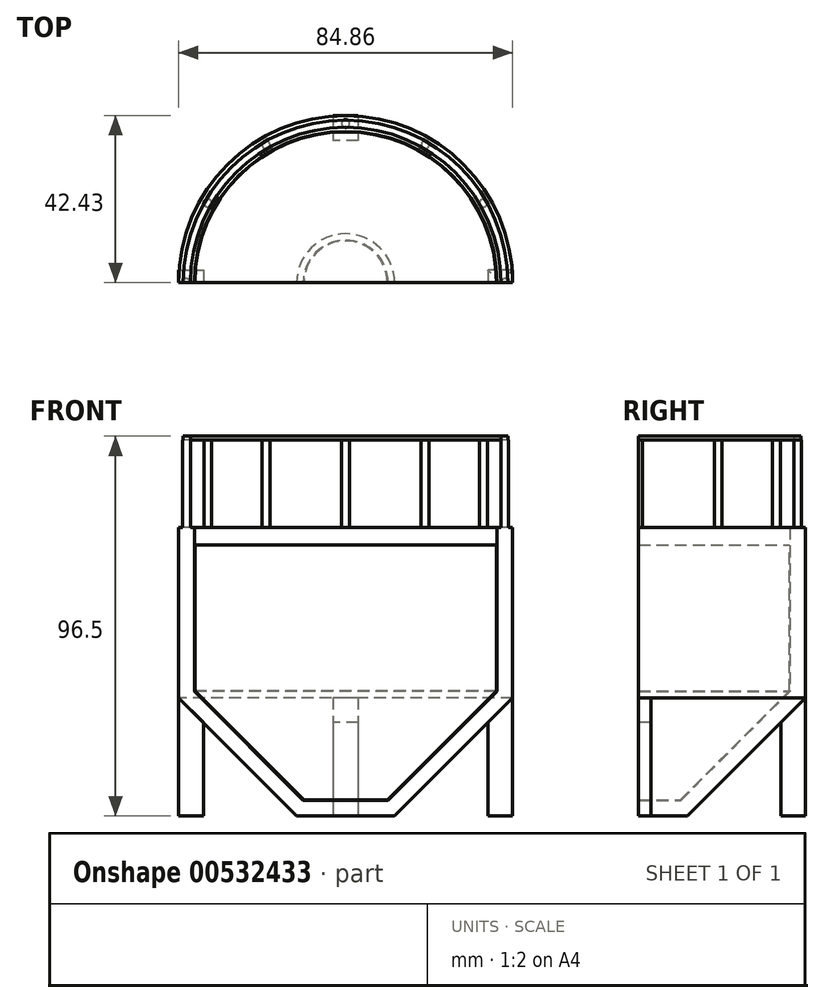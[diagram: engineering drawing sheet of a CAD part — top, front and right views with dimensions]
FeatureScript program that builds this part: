
annotation { "Feature Type Name" : "Feature", "Feature Type Description" : "" }
export const myFeature = defineFeature(function(context is Context, id is Id, definition is map)
    precondition{}
    {
        {
            var Q0;
            Q0=qCreatedBy(makeId("Top.planeOp"),FACE);
            var sketch = newSketch(context, id + "F0", { "sketchPlane" : qUnion([Q0])});
            skLineSegment(sketch, "E0", {"start": v(-29.35, 0) * mm, "end": v(28.84, 0) * mm, "construction": true});
            skLineSegment(sketch, "E1", {"start": v(0, 29.6) * mm, "end": v(0, -29.2) * mm, "construction": true});
            skLineSegment(sketch, "E2.bottom", {"start": v(30, 30) * mm, "end": v(-30, 30) * mm, "construction": true});
            skLineSegment(sketch, "E2.top", {"start": v(30, -30) * mm, "end": v(-30, -30) * mm, "construction": true});
            skLineSegment(sketch, "E2.left", {"start": v(30, 30) * mm, "end": v(30, -30) * mm, "construction": true});
            skLineSegment(sketch, "E2.right", {"start": v(-30, 30) * mm, "end": v(-30, -30) * mm, "construction": true});
            skPoint(sketch, "E2.middle", {"position": v(0, 0) * mm});
            skCircle(sketch, "E3", {"center": v(0, 0) * mm, "radius": 42.43 * mm});
            skSolve(sketch);
        }
        {
            var Q0;
            Q0 = qSketchRegion(id + "F0", true);
            extrude(context, id + "F1", {"entities" : qUnion([Q0]), "depth" : 73.3 * mm, "offsetDistance" : 25 * mm});
        }
        {
            var Q0;
            Q0=makeQuery(id+"F1.opExtrude","CAP_FACE",FACE,{"disambiguationData":[OSD([sQuery(id+"F0.wireOp",EDGE,"E3")])],"isStart":true});
            chamfer(context, id + "F2", {"entities" : qUnion([Q0]), "width" : 30 * mm, "tangentPropagation" : true});
        }
        {
            var Q0;
            Q0=makeQuery(id+"F1.opExtrude","CAP_FACE",FACE,{"disambiguationData":[OSD([sQuery(id+"F0.wireOp",EDGE,"E3")])],"isStart":false});
            shell(context, id + "F3", {"entities" : qUnion([Q0]), "thickness" : 4 * mm});
        }
        {
            var Q0;
            Q0=makeQuery(id+"F1.opExtrude","CAP_FACE",FACE,{"disambiguationData":[OSD([sQuery(id+"F0.wireOp",EDGE,"E3")])],"isStart":false});
            var sketch = newSketch(context, id + "F4", { "sketchPlane" : qUnion([Q0])});
            skCircle(sketch, "E4.0.0", {"center": v(0, 0) * mm, "radius": 42.43 * mm, "construction": true});
            skCircle(sketch, "E5.0", {"center": v(0, 0) * mm, "radius": 40.43 * mm, "construction": true});
            skCircle(sketch, "E6", {"center": v(0, 40.43) * mm, "radius": 1 * mm});
            skCircle(sketch, "E7.1.0", {"center": v(-20.21, 35.01) * mm, "radius": 1 * mm});
            skCircle(sketch, "E7.2.0", {"center": v(-35.01, 20.21) * mm, "radius": 1 * mm});
            skCircle(sketch, "E7.3.0", {"center": v(-40.43, 0) * mm, "radius": 1 * mm});
            skCircle(sketch, "E7.4.0", {"center": v(-35.01, -20.21) * mm, "radius": 1 * mm});
            skCircle(sketch, "E7.5.0", {"center": v(-20.21, -35.01) * mm, "radius": 1 * mm});
            skCircle(sketch, "E7.6.0", {"center": v(0, -40.43) * mm, "radius": 1 * mm});
            skCircle(sketch, "E7.7.0", {"center": v(20.21, -35.01) * mm, "radius": 1 * mm});
            skCircle(sketch, "E7.8.0", {"center": v(35.01, -20.21) * mm, "radius": 1 * mm});
            skCircle(sketch, "E7.9.0", {"center": v(40.43, 0) * mm, "radius": 1 * mm});
            skLineSegment(sketch, "E7.anchor1", {"start": v(0, 0) * mm, "end": v(0, 40.43) * mm, "construction": true});
            skLineSegment(sketch, "E7.anchor2", {"start": v(0, 0) * mm, "end": v(20.21, 35.01) * mm, "construction": true});
            skCircle(sketch, "E8.1.10.0", {"center": v(35.01, 20.21) * mm, "radius": 1 * mm});
            skCircle(sketch, "E9.1.11.0", {"center": v(20.21, 35.01) * mm, "radius": 1 * mm});
            skSolve(sketch);
        }
        {
            var Q0;
            Q0 = qSketchRegion(id + "F4", true);
            extrude(context, id + "F5", {"entities" : qUnion([Q0]), "operationType" : NewBodyOperationType.ADD, "depth" : 22.2 * mm, "offsetDistance" : 25 * mm});
        }
        {
            var Q0;
            Q0=makeQuery(id+"F5.opExtrude","CAP_FACE",FACE,{"disambiguationData":[OSD([sQuery(id+"F4.wireOp",EDGE,"E7.3.0")])],"isStart":false});
            var sketch = newSketch(context, id + "F6", { "sketchPlane" : qUnion([Q0])});
            skPoint(sketch, "E10.0", {"position": v(0, 0) * mm});
            skCircle(sketch, "E11", {"center": v(0, 0) * mm, "radius": 41.25 * mm});
            skCircle(sketch, "E12.0", {"center": v(0, 0) * mm, "radius": 39.45 * mm});
            skSolve(sketch);
        }
        {
            var Q0;
            Q0 = qSketchRegion(id + "F6", true);
            extrude(context, id + "F7", {"entities" : qUnion([Q0]), "operationType" : NewBodyOperationType.ADD, "depth" : 1 * mm, "offsetDistance" : 25 * mm});
        }
        {
            var Q0;
            Q0=qCreatedBy(makeId("Front.planeOp"),FACE);
            var sketch = newSketch(context, id + "F8", { "sketchPlane" : qUnion([Q0])});
            skLineSegment(sketch, "E13.0", {"start": v(-42.43, 30) * mm, "end": v(42.43, 30) * mm, "construction": true});
            skLineSegment(sketch, "E14", {"start": v(-12.43, 0) * mm, "end": v(-42.43, 30) * mm, "construction": true});
            skLineSegment(sketch, "E15.bottom", {"start": v(-42.43, 30) * mm, "end": v(-36.13, 30) * mm});
            skLineSegment(sketch, "E15.top", {"start": v(-42.43, 0) * mm, "end": v(-36.13, 0) * mm});
            skLineSegment(sketch, "E15.left", {"start": v(-42.43, 30) * mm, "end": v(-42.43, 0) * mm});
            skLineSegment(sketch, "E15.right", {"start": v(-36.13, 30) * mm, "end": v(-36.13, 0) * mm});
            skLineSegment(sketch, "E16.MirrorCS", {"start": v(36.13, 30) * mm, "end": v(36.13, 0) * mm});
            skLineSegment(sketch, "E17.MirrorCS", {"start": v(42.43, 30) * mm, "end": v(42.43, 0) * mm});
            skLineSegment(sketch, "E18.MirrorCS", {"start": v(42.43, 0) * mm, "end": v(36.13, 0) * mm});
            skLineSegment(sketch, "E19.MirrorCS", {"start": v(42.43, 30) * mm, "end": v(36.13, 30) * mm});
            skLineSegment(sketch, "E20.MirrorCS", {"start": v(12.43, 0) * mm, "end": v(42.43, 30) * mm, "construction": true});
            skLineSegment(sketch, "E21.MirrorCS", {"start": v(42.43, 30) * mm, "end": v(-42.43, 30) * mm, "construction": true});
            skLineSegment(sketch, "E22", {"start": v(42.43, 30) * mm, "end": v(36.13, 23.7) * mm});
            skLineSegment(sketch, "E23", {"start": v(-42.43, 30) * mm, "end": v(-36.13, 23.7) * mm});
            skSolve(sketch);
        }
        {
            var Q0;
            {var subQ0=sQuery(id+"F8.wireOp",EDGE,"E18.MirrorCS");Q0=makeQuery(id+"F8.imprint","IMPRINT",FACE,{"disambiguationData":[TD([[makeQuery(id+"F8.imprint","IMPRINT",EDGE,{"derivedFrom":subQ0}),-1.0]])]});}
            var Q1;
            {var subQ0=sQuery(id+"F8.wireOp",EDGE,"E15.top");Q1=makeQuery(id+"F8.imprint","IMPRINT",FACE,{"disambiguationData":[TD([[makeQuery(id+"F8.imprint","IMPRINT",EDGE,{"derivedFrom":subQ0}),1.0]])]});}
            extrude(context, id + "F9", {"entities" : qUnion([Q0, Q1]), "endBound" : BoundingType.SYMMETRIC, "depth" : 6.4 * mm, "offsetDistance" : 25 * mm});
        }
        {
            var Q0;
            Q0=makeQuery(id+"F9.opExtrude","SWEPT_BODY",BODY,{"disambiguationData":[OSD([sQuery(id+"F8.wireOp",EDGE,"E15.bottom"),sQuery(id+"F8.wireOp",EDGE,"E15.top"),sQuery(id+"F8.wireOp",EDGE,"E15.left"),sQuery(id+"F8.wireOp",EDGE,"E15.right")])]});
            var Q1;
            Q1=makeQuery(id+"F9.opExtrude","SWEPT_BODY",BODY,{"disambiguationData":[OSD([sQuery(id+"F8.wireOp",EDGE,"E18.MirrorCS"),sQuery(id+"F8.wireOp",EDGE,"E19.MirrorCS"),sQuery(id+"F8.wireOp",EDGE,"E17.MirrorCS"),sQuery(id+"F8.wireOp",EDGE,"E16.MirrorCS")])]});
            var Q2;
            {var subQ0=sQuery(id+"F0.wireOp",EDGE,"E3");Q2=makeQuery(id+"F2.opChamfer","BLEND_EDGE",EDGE,{"blendedFrom":[makeQuery(id+"F1.opExtrude","CAP_EDGE",EDGE,{"disambiguationData":[OSD([subQ0])],"isStart":true}),makeQuery(id+"F1.opExtrude","CAP_FACE",FACE,{"disambiguationData":[OSD([subQ0])],"isStart":true})],"blendedInto":[makeQuery(id+"F1.opExtrude","CAP_FACE",FACE,{"disambiguationData":[OSD([subQ0])],"isStart":true})]});}
            circularPattern(context, id + "F10", {"entities" : qUnion([Q0, Q1]), "axis" : qUnion([Q2]), "angle" : 180 * degree, "instanceCount" : 3, "equalSpace" : true});
        }
        {
            var Q0;
            Q0=qCreatedBy(makeId("Front.planeOp"),FACE);
            var sketch = newSketch(context, id + "F11", { "sketchPlane" : qUnion([Q0])});
            skLineSegment(sketch, "E24", {"start": v(-38.3, 68.88) * mm, "end": v(-38.3, 31.75) * mm});
            skLineSegment(sketch, "E25", {"start": v(-38.3, 31.75) * mm, "end": v(-10.59, 4.03) * mm});
            skLineSegment(sketch, "E26", {"start": v(-10.59, 4.03) * mm, "end": v(0, 4.03) * mm});
            skLineSegment(sketch, "E27", {"start": v(0, 4.03) * mm, "end": v(0, 68.88) * mm});
            skLineSegment(sketch, "E28", {"start": v(0, 68.88) * mm, "end": v(-38.3, 68.88) * mm});
            skSolve(sketch);
        }
        {
            var Q0;
            Q0 = qSketchRegion(id + "F11", true);
            var Q1;
            {var subQ0=sQuery(id+"F0.wireOp",EDGE,"E3");Q1=makeQuery(id+"F3.opShell","OFFSET_FACE",FACE,{"disambiguationData":[OSD([subQ0]),TDD([makeQuery(id+"F2.opChamfer","BLEND_FACE",FACE,{"disambiguationData":[OSD([subQ0])]})])]});}
            revolve(context, id + "F12", {"entities" : qUnion([Q0]), "axis" : qUnion([Q1]), "revolveType" : RevolveType.FULL});
        }
        {
            var Q0;
            Q0=qCreatedBy(makeId("Top.planeOp"),FACE);
            var sketch = newSketch(context, id + "F13", { "sketchPlane" : qUnion([Q0])});
            skLineSegment(sketch, "E29", {"start": v(-50, 0) * mm, "end": v(50, 0) * mm, "construction": true});
            skLineSegment(sketch, "E30.bottom", {"start": v(-50, 0) * mm, "end": v(50, 0) * mm});
            skLineSegment(sketch, "E30.top", {"start": v(-50, -50) * mm, "end": v(50, -50) * mm});
            skLineSegment(sketch, "E30.left", {"start": v(-50, 0) * mm, "end": v(-50, -50) * mm});
            skLineSegment(sketch, "E30.right", {"start": v(50, 0) * mm, "end": v(50, -50) * mm});
            skSolve(sketch);
        }
        {
            var Q0;
            Q0=makeQuery(id+"F10.opPattern","COPY",FACE,{"derivedFrom":makeQuery(id+"F9.opExtrude","SWEPT_FACE",FACE,{"disambiguationData":[OSD([sQuery(id+"F8.wireOp",EDGE,"E15.top")])]}),"instanceName":"2"});
            fillet(context, id + "F14", {"entities" : qUnion([Q0]), "radius" : .8 * mm, "tangentPropagation" : true, "allowEdgeOverflow" : false});
        }
        {
            var Q0;
            Q0 = qSketchRegion(id + "F13", true);
            extrude(context, id + "F15", {"entities" : qUnion([Q0]), "operationType" : NewBodyOperationType.REMOVE, "depth" : 200 * mm, "offsetDistance" : 25 * mm});
        }
    });
